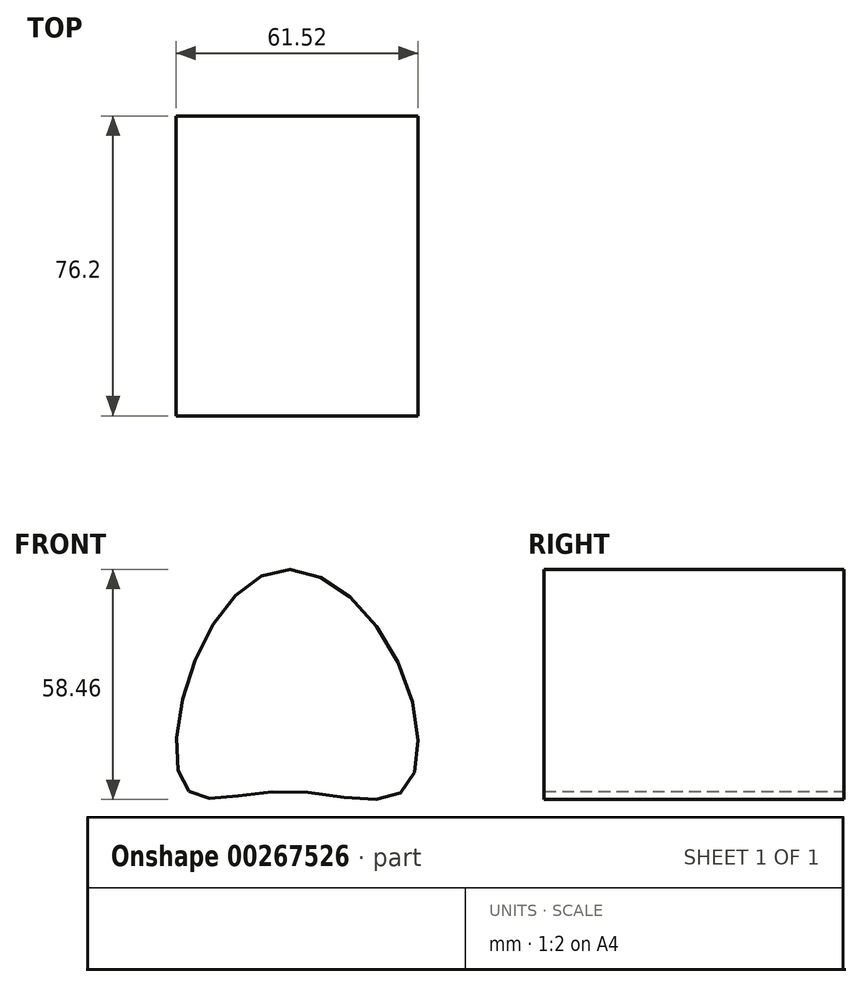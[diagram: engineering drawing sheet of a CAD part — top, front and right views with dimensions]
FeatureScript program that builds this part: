
annotation { "Feature Type Name" : "Feature", "Feature Type Description" : "" }
export const myFeature = defineFeature(function(context is Context, id is Id, definition is map)
    precondition{}
    {
        {
            var Q0;
            Q0=qCreatedBy(makeId("Front.planeOp"),FACE);
            var sketch = newSketch(context, id + "F0", { "sketchPlane" : qUnion([Q0])});
            skFitSpline(sketch, "E0", {"points": [v(-24.44, 0) * mm, v(-23.45, 31.93) * mm, v(0, 56.36) * mm, v(28.58, 32.91) * mm, v(29.76, 0) * mm, v(0, 0) * mm, v(-24.44, 0) * mm]});
            skSolve(sketch);
        }
        {
            var Q0;
            Q0 = qSketchRegion(id + "F0", true);
            extrude(context, id + "F1", {"entities" : qUnion([Q0]), "depth" : 76.2 * mm});
        }
    });
